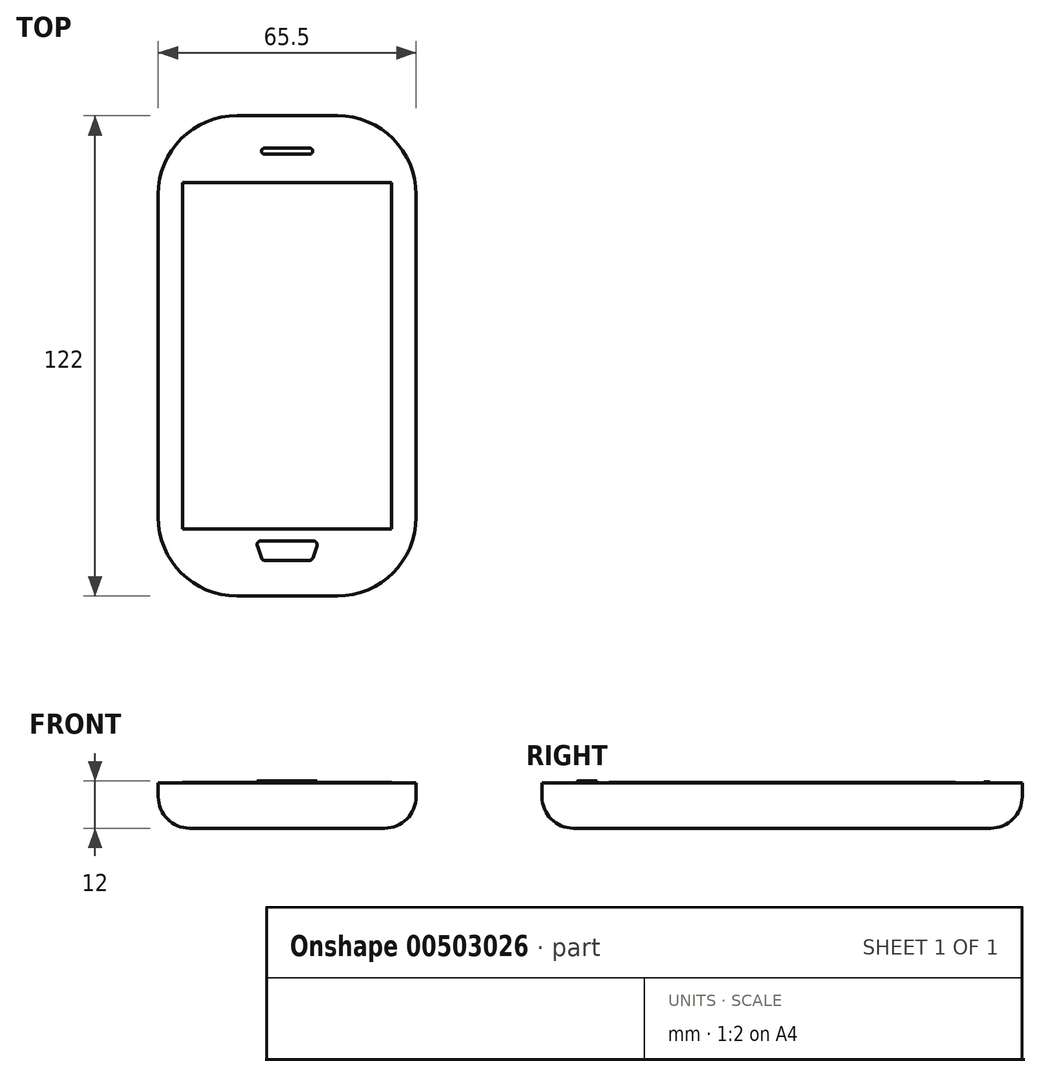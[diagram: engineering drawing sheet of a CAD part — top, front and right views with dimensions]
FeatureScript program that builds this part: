
annotation { "Feature Type Name" : "Feature", "Feature Type Description" : "" }
export const myFeature = defineFeature(function(context is Context, id is Id, definition is map)
    precondition{}
    {
        {
            var Q0;
            Q0=qCreatedBy(makeId("Top.planeOp"),FACE);
            var sketch = newSketch(context, id + "F0", { "sketchPlane" : qUnion([Q0])});
            skLineSegment(sketch, "E0.bottom", {"start": v(12.75, 61) * mm, "end": v(-12.75, 61) * mm});
            skLineSegment(sketch, "E0.top", {"start": v(12.75, -61) * mm, "end": v(-12.75, -61) * mm});
            skLineSegment(sketch, "E0.left", {"start": v(32.75, 41) * mm, "end": v(32.75, -41) * mm});
            skLineSegment(sketch, "E0.right", {"start": v(-32.75, 41) * mm, "end": v(-32.75, -41) * mm});
            skPoint(sketch, "E0.middle", {"position": v(0, 0) * mm});
            skPoint(sketch, "E1.visualSharp", {"position": v(32.75, 61) * mm});
            skArc(sketch, "E1.filletArc", {"start": v(32.75, 41) * mm, "mid": v(26.9, 55.14) * mm, "end": v(12.75, 61) * mm});
            skPoint(sketch, "E2.visualSharp", {"position": v(-32.75, 61) * mm});
            skArc(sketch, "E2.filletArc", {"start": v(-12.75, 61) * mm, "mid": v(-26.9, 55.14) * mm, "end": v(-32.75, 41) * mm});
            skPoint(sketch, "E3.visualSharp", {"position": v(-32.75, -61) * mm});
            skArc(sketch, "E3.filletArc", {"start": v(-32.75, -41) * mm, "mid": v(-26.9, -55.14) * mm, "end": v(-12.75, -61) * mm});
            skPoint(sketch, "E4.visualSharp", {"position": v(32.75, -61) * mm});
            skArc(sketch, "E4.filletArc", {"start": v(12.75, -61) * mm, "mid": v(26.9, -55.14) * mm, "end": v(32.75, -41) * mm});
            skSolve(sketch);
        }
        {
            var Q0;
            Q0=makeQuery(id+"F0.imprint","IMPRINT",FACE,{"disambiguationData":[TD([[makeQuery(id+"F0.imprint","IMPRINT",EDGE,{"derivedFrom":sQuery(id+"F0.wireOp",EDGE,"E0.bottom")}),1.0]])]});
            extrude(context, id + "F1", {"entities" : qUnion([Q0]), "depth" : 11.5 * mm});
        }
        {
            var Q0;
            Q0=makeQuery(id+"F1.opExtrude","CAP_EDGE",EDGE,{"disambiguationData":[OSD([sQuery(id+"F0.wireOp",EDGE,"E2.filletArc")])],"isStart":true});
            fillet(context, id + "F2", {"entities" : qUnion([Q0]), "radius" : 8 * mm, "tangentPropagation" : true, "allowEdgeOverflow" : false});
        }
        {
            var Q0;
            Q0=makeQuery(id+"F1.opExtrude","CAP_FACE",FACE,{"disambiguationData":[OSD([sQuery(id+"F0.wireOp",EDGE,"E0.bottom"),sQuery(id+"F0.wireOp",EDGE,"E0.top"),sQuery(id+"F0.wireOp",EDGE,"E0.left"),sQuery(id+"F0.wireOp",EDGE,"E0.right"),sQuery(id+"F0.wireOp",EDGE,"E1.filletArc"),sQuery(id+"F0.wireOp",EDGE,"E2.filletArc"),sQuery(id+"F0.wireOp",EDGE,"E3.filletArc"),sQuery(id+"F0.wireOp",EDGE,"E4.filletArc")])],"isStart":false});
            var sketch = newSketch(context, id + "F3", { "sketchPlane" : qUnion([Q0])});
            skLineSegment(sketch, "E5.bottom", {"start": v(-6.6, -47) * mm, "end": v(0, -47) * mm});
            skLineSegment(sketch, "E5.top", {"start": v(-5.6, -52) * mm, "end": v(0, -52) * mm});
            skPoint(sketch, "E5.middle", {"position": v(0, -46.07) * mm});
            skLineSegment(sketch, "E6", {"start": v(-7.56, -48.32) * mm, "end": v(-6.54, -51.32) * mm});
            skArc(sketch, "E7.filletArc", {"start": v(-6.6, -47) * mm, "mid": v(-7.42, -47.42) * mm, "end": v(-7.56, -48.32) * mm});
            skArc(sketch, "E8.filletArc", {"start": v(-6.54, -51.32) * mm, "mid": v(-6.18, -51.81) * mm, "end": v(-5.6, -52) * mm});
            skLineSegment(sketch, "E9", {"start": v(0, -41.9) * mm, "end": v(0, -50.7) * mm, "construction": true});
            skLineSegment(sketch, "E10.MirrorCS", {"start": v(7.56, -48.32) * mm, "end": v(6.54, -51.32) * mm});
            skLineSegment(sketch, "E11.MirrorCS", {"start": v(5.6, -52) * mm, "end": v(0, -52) * mm});
            skLineSegment(sketch, "E12.MirrorCS", {"start": v(6.6, -47) * mm, "end": v(0, -47) * mm});
            skArc(sketch, "E13.MirrorCS", {"start": v(6.54, -51.32) * mm, "mid": v(6.18, -51.81) * mm, "end": v(5.6, -52) * mm});
            skArc(sketch, "E14.MirrorCS", {"start": v(6.6, -47) * mm, "mid": v(7.42, -47.42) * mm, "end": v(7.56, -48.32) * mm});
            skSolve(sketch);
        }
        {
            var Q0;
            Q0=makeQuery(id+"F3.imprint","IMPRINT",FACE,{"disambiguationData":[TD([[makeQuery(id+"F3.imprint","IMPRINT",EDGE,{"derivedFrom":sQuery(id+"F3.wireOp",EDGE,"E5.bottom")}),-1.0]])]});
            extrude(context, id + "F4", {"entities" : qUnion([Q0]), "operationType" : NewBodyOperationType.ADD, "depth" : 0.5 * mm});
        }
        {
            var Q0;
            Q0=makeQuery(id+"F1.opExtrude","CAP_FACE",FACE,{"disambiguationData":[OSD([sQuery(id+"F0.wireOp",EDGE,"E0.bottom"),sQuery(id+"F0.wireOp",EDGE,"E0.top"),sQuery(id+"F0.wireOp",EDGE,"E0.left"),sQuery(id+"F0.wireOp",EDGE,"E0.right"),sQuery(id+"F0.wireOp",EDGE,"E1.filletArc"),sQuery(id+"F0.wireOp",EDGE,"E2.filletArc"),sQuery(id+"F0.wireOp",EDGE,"E3.filletArc"),sQuery(id+"F0.wireOp",EDGE,"E4.filletArc")])],"isStart":false});
            var sketch = newSketch(context, id + "F5", { "sketchPlane" : qUnion([Q0])});
            skLineSegment(sketch, "E15.bottom", {"start": v(26.5, 44) * mm, "end": v(-26.5, 44) * mm});
            skLineSegment(sketch, "E15.top", {"start": v(26.5, -44) * mm, "end": v(-26.5, -44) * mm});
            skLineSegment(sketch, "E15.left", {"start": v(26.5, 44) * mm, "end": v(26.5, -44) * mm});
            skLineSegment(sketch, "E15.right", {"start": v(-26.5, 44) * mm, "end": v(-26.5, -44) * mm});
            skPoint(sketch, "E15.middle", {"position": v(0, 0) * mm});
            skSolve(sketch);
        }
        {
            var Q0;
            Q0=makeQuery(id+"F5.imprint","IMPRINT",FACE,{"disambiguationData":[TD([[makeQuery(id+"F5.imprint","IMPRINT",EDGE,{"derivedFrom":sQuery(id+"F5.wireOp",EDGE,"E15.bottom")}),1.0]])]});
            extrude(context, id + "F6", {"entities" : qUnion([Q0]), "operationType" : NewBodyOperationType.ADD, "depth" : 0.1 * mm});
        }
        {
            var Q0;
            Q0=makeQuery(id+"F1.opExtrude","CAP_FACE",FACE,{"disambiguationData":[OSD([sQuery(id+"F0.wireOp",EDGE,"E0.bottom"),sQuery(id+"F0.wireOp",EDGE,"E0.top"),sQuery(id+"F0.wireOp",EDGE,"E0.left"),sQuery(id+"F0.wireOp",EDGE,"E0.right"),sQuery(id+"F0.wireOp",EDGE,"E1.filletArc"),sQuery(id+"F0.wireOp",EDGE,"E2.filletArc"),sQuery(id+"F0.wireOp",EDGE,"E3.filletArc"),sQuery(id+"F0.wireOp",EDGE,"E4.filletArc")])],"isStart":false});
            var sketch = newSketch(context, id + "F7", { "sketchPlane" : qUnion([Q0])});
            skLineSegment(sketch, "E16.bottom", {"start": v(5.75, 51.25) * mm, "end": v(-5.75, 51.25) * mm});
            skLineSegment(sketch, "E16.top", {"start": v(5.75, 52.75) * mm, "end": v(-5.75, 52.75) * mm});
            skLineSegment(sketch, "E16.left", {"start": v(6.5, 52) * mm, "end": v(6.5, 52) * mm});
            skLineSegment(sketch, "E16.right", {"start": v(-6.5, 52) * mm, "end": v(-6.5, 52) * mm});
            skPoint(sketch, "E16.middle", {"position": v(0, 52) * mm});
            skPoint(sketch, "E17.visualSharp", {"position": v(-6.5, 52.75) * mm});
            skArc(sketch, "E17.filletArc", {"start": v(-5.75, 52.75) * mm, "mid": v(-6.28, 52.53) * mm, "end": v(-6.5, 52) * mm});
            skPoint(sketch, "E18.visualSharp", {"position": v(-6.5, 51.25) * mm});
            skArc(sketch, "E18.filletArc", {"start": v(-6.5, 52) * mm, "mid": v(-6.28, 51.47) * mm, "end": v(-5.75, 51.25) * mm});
            skPoint(sketch, "E19.visualSharp", {"position": v(6.5, 52.75) * mm});
            skArc(sketch, "E19.filletArc", {"start": v(6.5, 52) * mm, "mid": v(6.28, 52.53) * mm, "end": v(5.75, 52.75) * mm});
            skPoint(sketch, "E20.visualSharp", {"position": v(6.5, 51.25) * mm});
            skArc(sketch, "E20.filletArc", {"start": v(5.75, 51.25) * mm, "mid": v(6.28, 51.47) * mm, "end": v(6.5, 52) * mm});
            skSolve(sketch);
        }
        {
            var Q0;
            Q0=makeQuery(id+"F7.imprint","IMPRINT",FACE,{"disambiguationData":[TD([[makeQuery(id+"F7.imprint","IMPRINT",EDGE,{"derivedFrom":sQuery(id+"F7.wireOp",EDGE,"E16.bottom")}),-1.0]])]});
            extrude(context, id + "F8", {"entities" : qUnion([Q0]), "operationType" : NewBodyOperationType.ADD, "depth" : 0.2 * mm});
        }
    });
